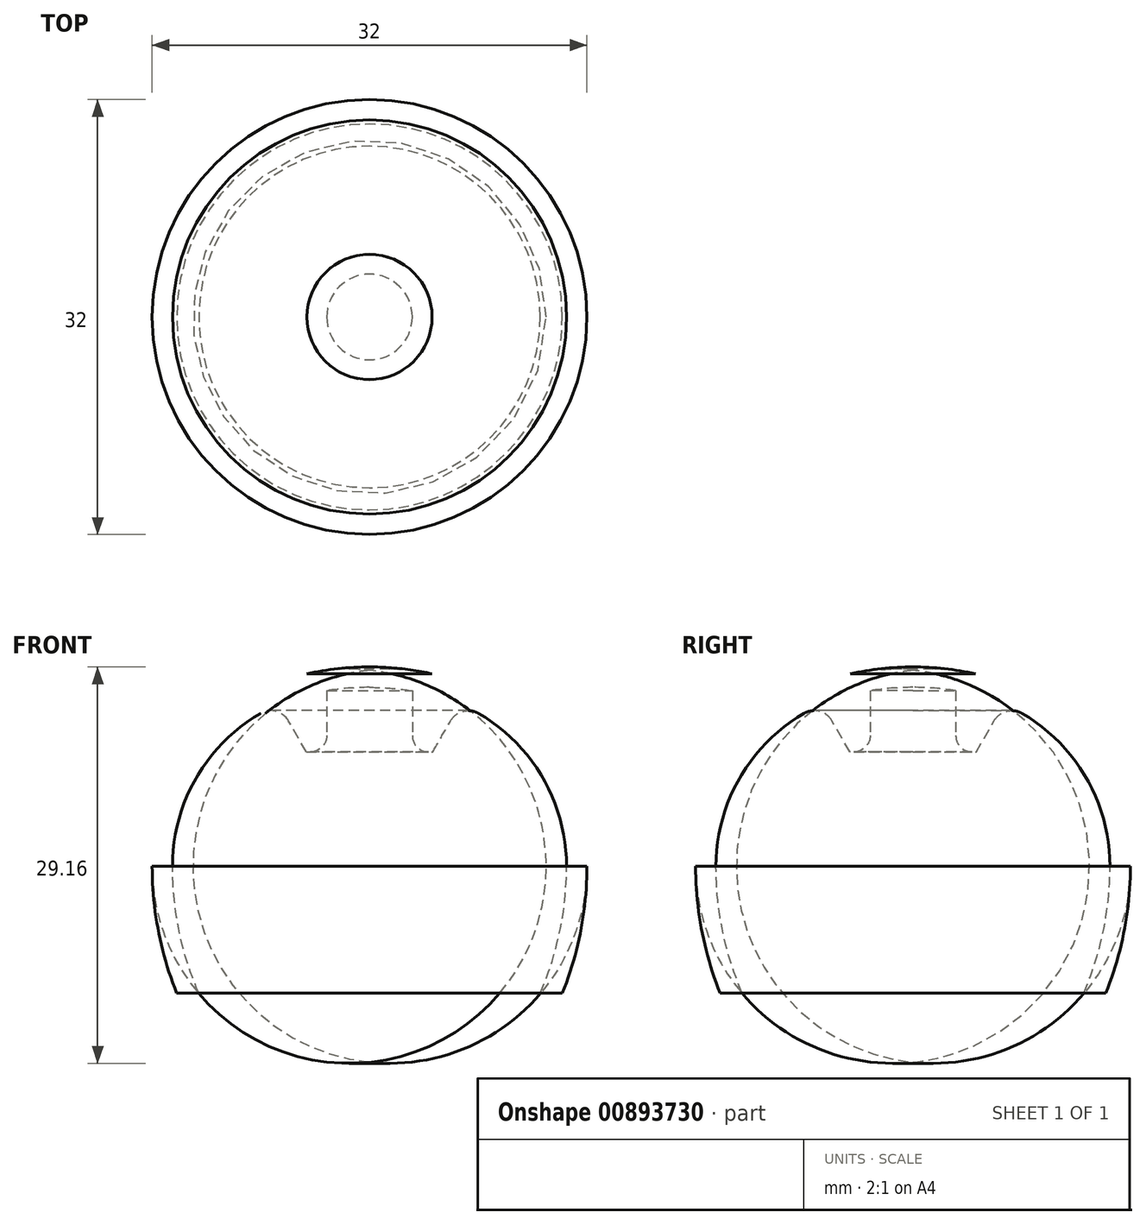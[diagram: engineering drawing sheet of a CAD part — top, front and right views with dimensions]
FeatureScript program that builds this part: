
annotation { "Feature Type Name" : "Feature", "Feature Type Description" : "" }
export const myFeature = defineFeature(function(context is Context, id is Id, definition is map)
    precondition{}
    {
        {
            var Q0;
            Q0=qCreatedBy(makeId("Front.planeOp"),FACE);
            var sketch = newSketch(context, id + "F0", { "sketchPlane" : qUnion([Q0])});
            skLineSegment(sketch, "E0", {"start": v(-4.65, 21.95) * mm, "end": v(-4.65, 17.75) * mm});
            skLineSegment(sketch, "E1", {"start": v(-4.65, 17.75) * mm, "end": v(-3.15, 17.75) * mm});
            skLineSegment(sketch, "E2", {"start": v(-3.15, 17.75) * mm, "end": v(-3.15, 22.25) * mm});
            skLineSegment(sketch, "E3", {"start": v(0, 22.5) * mm, "end": v(0, 24) * mm});
            skLineSegment(sketch, "E4", {"start": v(-4.65, 17.75) * mm, "end": v(-6.72, 21.34) * mm});
            skArc(sketch, "E5", {"start": v(0, 22.5) * mm, "mid": v(-2.16, 22.38) * mm, "end": v(-4.29, 22.04) * mm});
            skLineSegment(sketch, "E6", {"start": v(0, 22.5) * mm, "end": v(-14.5, 22.5) * mm, "construction": true});
            skLineSegment(sketch, "E7", {"start": v(-14.5, 22.5) * mm, "end": v(-14.5, 0) * mm, "construction": true});
            skArc(sketch, "E8", {"start": v(-4.29, 22.04) * mm, "mid": v(-11.63, 17.49) * mm, "end": v(-14.5, 9.34) * mm});
            skArc(sketch, "E9", {"start": v(-14.5, 9.34) * mm, "mid": v(-14.01, 4.57) * mm, "end": v(-12.57, 0) * mm});
            skArc(sketch, "E10.0", {"start": v(-16, 9.34) * mm, "mid": v(-15.54, 4.58) * mm, "end": v(-14.2, 0) * mm});
            skArc(sketch, "E10.1", {"start": v(-4.6, 23.5) * mm, "mid": v(-12.8, 18.43) * mm, "end": v(-16, 9.34) * mm});
            skArc(sketch, "E10.2", {"start": v(0, 24) * mm, "mid": v(-2.32, 23.87) * mm, "end": v(-4.6, 23.5) * mm});
            skLineSegment(sketch, "E11", {"start": v(-14.2, 0) * mm, "end": v(-12.57, 0) * mm});
            skLineSegment(sketch, "E12", {"start": v(-12.57, 0) * mm, "end": v(20.13, 14.16) * mm, "construction": true});
            skLineSegment(sketch, "E13", {"start": v(-14.5, 9.34) * mm, "end": v(25.06, 9.34) * mm, "construction": true});
            skLineSegment(sketch, "E14", {"start": v(-4.29, 22.04) * mm, "end": v(1.86, -6) * mm, "construction": true});
            skSolve(sketch);
        }
        {
            var Q0;
            Q0=qSketchRegion(id+"F0",true);
            var Q1;
            Q1=sQuery(id+"F0.wireOp",EDGE,"E3");
            revolve(context, id + "F1", {"surfaceOperationType" : NewSurfaceOperationType.NEW, "entities" : qUnion([Q0]), "axis" : qUnion([Q1]), "revolveType" : RevolveType.FULL});
        }
        {
            var Q0;
            Q0=makeQuery(id+"F1.opRevolve","SWEPT_EDGE",EDGE,{"disambiguationData":[OSD([sQuery(id+"F0.wireOp",EDGE,"E1"),sQuery(id+"F0.wireOp",EDGE,"E2")])]});
            fillet(context, id + "F2", {"entities" : qUnion([Q0]), "radius" : 1.2 * mm, "tangentPropagation" : true, "allowEdgeOverflow" : false});
        }
        {
            var Q0;
            Q0=makeQuery(id+"F1.opRevolve","SWEPT_EDGE",EDGE,{"disambiguationData":[OSD([sQuery(id+"F0.wireOp",EDGE,"507aa7eb-6e30-4b8d-87b6-53970dac25a2.0"),sQuery(id+"F0.wireOp",EDGE,"E4")])]});
            fillet(context, id + "F3", {"entities" : qUnion([Q0]), "radius" : 1.5 * mm, "tangentPropagation" : true, "allowEdgeOverflow" : false});
        }
    });
